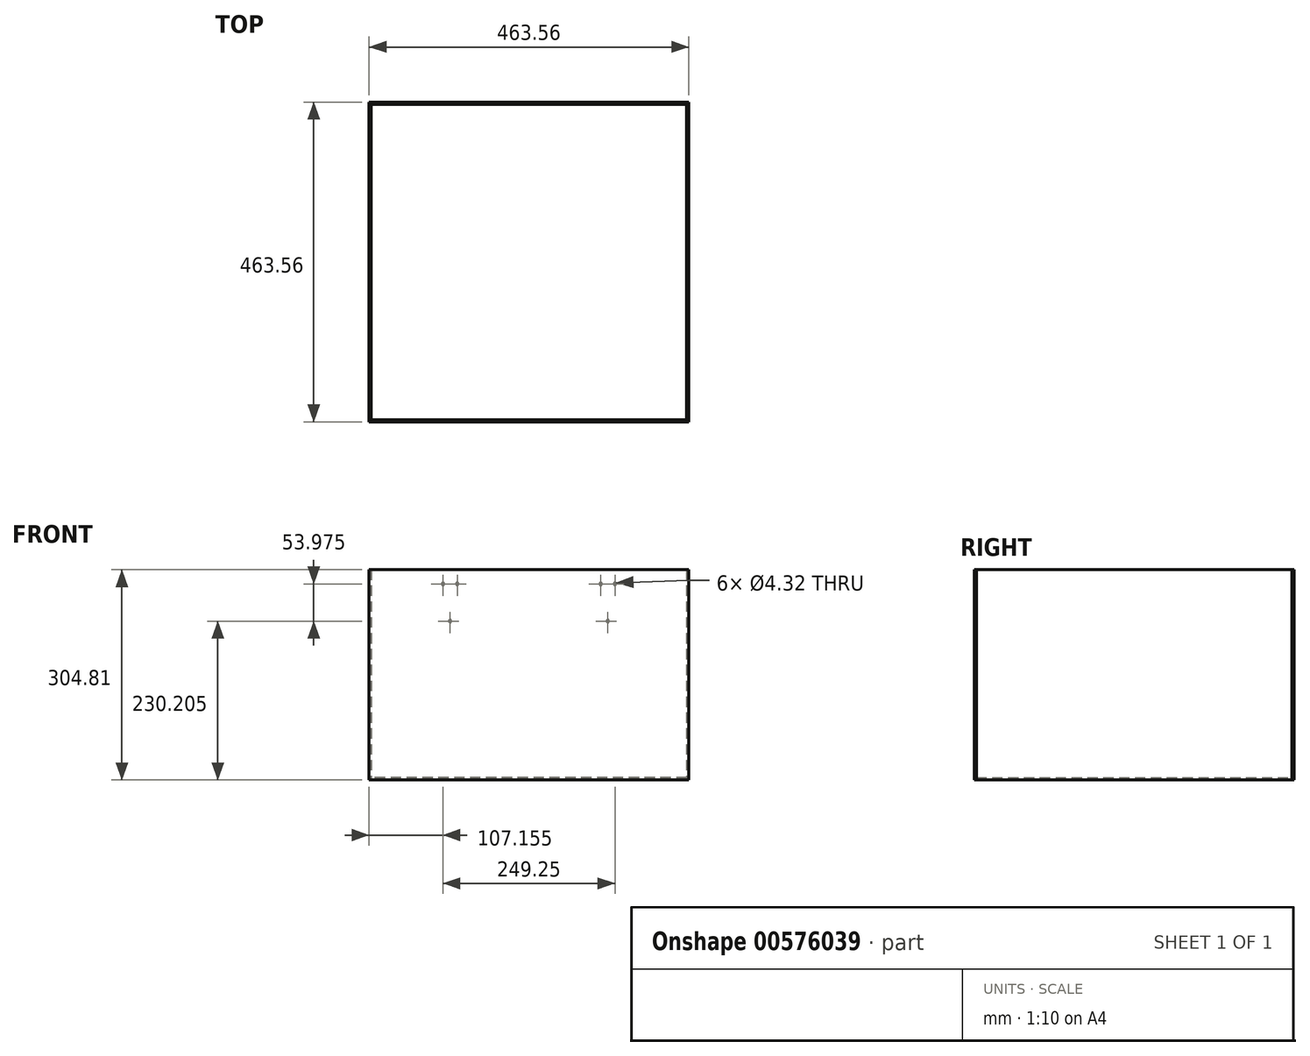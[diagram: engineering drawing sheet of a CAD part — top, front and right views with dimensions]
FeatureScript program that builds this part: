
annotation { "Feature Type Name" : "Feature", "Feature Type Description" : "" }
export const myFeature = defineFeature(function(context is Context, id is Id, definition is map)
    precondition{}
    {
        {
            var Q0;
            Q0=qCreatedBy(makeId("Top.planeOp"),FACE);
            var sketch = newSketch(context, id + "F0", { "sketchPlane" : qUnion([Q0])});
            skLineSegment(sketch, "E0.bottom", {"start": v(228.6, -228.6) * mm, "end": v(-228.6, -228.6) * mm});
            skLineSegment(sketch, "E0.top", {"start": v(228.6, 228.6) * mm, "end": v(-228.6, 228.6) * mm});
            skLineSegment(sketch, "E0.left", {"start": v(228.6, -228.6) * mm, "end": v(228.6, 228.6) * mm});
            skLineSegment(sketch, "E0.right", {"start": v(-228.6, -228.6) * mm, "end": v(-228.6, 228.6) * mm});
            skPoint(sketch, "E0.middle", {"position": v(0, 0) * mm});
            skSolve(sketch);
        }
        {
            var Q0;
            Q0=qSketchRegion(id+"F0",true);
            extrude(context, id + "F1", {"entities" : qUnion([Q0]), "depth" : 3.17 * mm, "offsetDistance" : 25.4 * mm});
        }
        {
            var Q0;
            Q0=makeQuery(id+"F1.opExtrude","SWEPT_FACE",FACE,{"disambiguationData":[OSD([sQuery(id+"F0.wireOp",EDGE,"E0.left")])]});
            var sketch = newSketch(context, id + "F2", { "sketchPlane" : qUnion([Q0])});
            skLineSegment(sketch, "E1", {"start": v(-228.6, 0) * mm, "end": v(-228.6, 3.18) * mm});
            skLineSegment(sketch, "E2", {"start": v(-228.6, 3.18) * mm, "end": v(-228.6, 307.98) * mm});
            skLineSegment(sketch, "E3", {"start": v(-228.6, 307.98) * mm, "end": v(228.6, 307.98) * mm});
            skLineSegment(sketch, "E4", {"start": v(228.6, 307.98) * mm, "end": v(228.6, 3.18) * mm});
            skLineSegment(sketch, "E5", {"start": v(228.6, 3.18) * mm, "end": v(228.6, 0) * mm});
            skLineSegment(sketch, "E6", {"start": v(228.6, 0) * mm, "end": v(-228.6, 0) * mm});
            skSolve(sketch);
        }
        {
            var Q0;
            Q0=qSketchRegion(id+"F2",true);
            extrude(context, id + "F3", {"entities" : qUnion([Q0]), "depth" : 3.17 * mm, "offsetDistance" : 25.4 * mm});
        }
        {
            var Q0;
            Q0=makeQuery(id+"F3.opExtrude","SWEPT_BODY",BODY,{"disambiguationData":[OSD([sQuery(id+"F2.wireOp",EDGE,"E1"),sQuery(id+"F2.wireOp",EDGE,"E2"),sQuery(id+"F2.wireOp",EDGE,"E3"),sQuery(id+"F2.wireOp",EDGE,"E4"),sQuery(id+"F2.wireOp",EDGE,"E5"),sQuery(id+"F2.wireOp",EDGE,"E6")])]});
            var Q1;
            Q1=qCreatedBy(makeId("Right.planeOp"),FACE);
            mirror(context, id + "F4", {"entities" : qUnion([Q0]), "mirrorPlane" : qUnion([Q1])});
        }
        {
            var Q0;
            Q0=makeQuery(id+"F1.opExtrude","SWEPT_FACE",FACE,{"disambiguationData":[OSD([sQuery(id+"F0.wireOp",EDGE,"E0.bottom")])]});
            var sketch = newSketch(context, id + "F5", { "sketchPlane" : qUnion([Q0])});
            skLineSegment(sketch, "E7", {"start": v(-231.78, 0) * mm, "end": v(-231.78, 307.98) * mm});
            skLineSegment(sketch, "E8", {"start": v(-231.78, 307.98) * mm, "end": v(231.77, 307.98) * mm});
            skLineSegment(sketch, "E9", {"start": v(231.77, 307.98) * mm, "end": v(231.77, 0) * mm});
            skLineSegment(sketch, "E10", {"start": v(-231.78, 0) * mm, "end": v(231.77, 0) * mm});
            skSolve(sketch);
        }
        {
            var Q0;
            Q0=qSketchRegion(id+"F5",true);
            extrude(context, id + "F6", {"entities" : qUnion([Q0]), "depth" : 3.17 * mm, "offsetDistance" : 25.4 * mm});
        }
        {
            var Q0;
            Q0=makeQuery(id+"F6.opExtrude","SWEPT_BODY",BODY,{"disambiguationData":[OSD([sQuery(id+"F5.wireOp",EDGE,"E7"),sQuery(id+"F5.wireOp",EDGE,"E8"),sQuery(id+"F5.wireOp",EDGE,"E9"),sQuery(id+"F5.wireOp",EDGE,"E10")])]});
            var Q1;
            Q1=qCreatedBy(makeId("Front.planeOp"),FACE);
            mirror(context, id + "F7", {"entities" : qUnion([Q0]), "mirrorPlane" : qUnion([Q1])});
        }
        {
            var Q0;
            Q0=makeQuery(id+"F7.opPattern","COPY",FACE,{"derivedFrom":makeQuery(id+"F6.opExtrude","CAP_FACE",FACE,{"disambiguationData":[OSD([sQuery(id+"F5.wireOp",EDGE,"E7"),sQuery(id+"F5.wireOp",EDGE,"E8"),sQuery(id+"F5.wireOp",EDGE,"E9"),sQuery(id+"F5.wireOp",EDGE,"E10")])],"isStart":true}),"instanceName":"1"});
            var sketch = newSketch(context, id + "F8", { "sketchPlane" : qUnion([Q0])});
            skLineSegment(sketch, "E11", {"start": v(-228.6, 307.98) * mm, "end": v(-152.4, 307.98) * mm});
            skLineSegment(sketch, "E12", {"start": v(-152.4, 307.98) * mm, "end": v(-114.3, 307.98) * mm});
            skLineSegment(sketch, "E13", {"start": v(-114.3, 307.98) * mm, "end": v(-114.3, 287.35) * mm});
            skLineSegment(sketch, "E14", {"start": v(-114.3, 287.35) * mm, "end": v(-114.3, 233.38) * mm});
            skLineSegment(sketch, "E15", {"start": v(-114.3, 287.35) * mm, "end": v(-103.97, 287.35) * mm});
            skLineSegment(sketch, "E16", {"start": v(-228.6, 307.98) * mm, "end": v(0, 307.98) * mm});
            skLineSegment(sketch, "E17", {"start": v(0, 307.98) * mm, "end": v(0, 430.1) * mm});
            skLineSegment(sketch, "E18.MirrorCS", {"start": v(-114.3, 287.35) * mm, "end": v(-124.63, 287.35) * mm});
            skLineSegment(sketch, "E19.MirrorCS", {"start": v(152.4, 307.98) * mm, "end": v(114.3, 307.98) * mm});
            skLineSegment(sketch, "E20.MirrorCS", {"start": v(228.6, 307.98) * mm, "end": v(152.4, 307.98) * mm});
            skLineSegment(sketch, "E21.MirrorCS", {"start": v(228.6, 307.98) * mm, "end": v(0, 307.98) * mm});
            skLineSegment(sketch, "E22.MirrorCS", {"start": v(114.3, 287.35) * mm, "end": v(124.63, 287.35) * mm});
            skLineSegment(sketch, "E23.MirrorCS", {"start": v(114.3, 287.35) * mm, "end": v(103.97, 287.35) * mm});
            skLineSegment(sketch, "E24.MirrorCS", {"start": v(114.3, 287.35) * mm, "end": v(114.3, 233.38) * mm});
            skLineSegment(sketch, "E25.MirrorCS", {"start": v(114.3, 307.98) * mm, "end": v(114.3, 287.35) * mm});
            skSolve(sketch);
        }
        {
            var Q0;
            Q0=sQuery(id+"F8.wireOp",VERTEX,"E23.MirrorCS.end");
            var Q1;
            Q1=sQuery(id+"F8.wireOp",VERTEX,"E22.MirrorCS.end");
            var Q2;
            Q2=sQuery(id+"F8.wireOp",VERTEX,"E24.MirrorCS.end");
            var Q3;
            Q3=sQuery(id+"F8.wireOp",VERTEX,"E14.end");
            var Q4;
            Q4=sQuery(id+"F8.wireOp",VERTEX,"E18.MirrorCS.end");
            var Q5;
            Q5=sQuery(id+"F8.wireOp",VERTEX,"E15.end");
            var Q6;
            Q6=makeQuery(id+"F7.opPattern","COPY",BODY,{"derivedFrom":makeQuery(id+"F6.opExtrude","SWEPT_BODY",BODY,{"disambiguationData":[OSD([sQuery(id+"F5.wireOp",EDGE,"E7"),sQuery(id+"F5.wireOp",EDGE,"E8"),sQuery(id+"F5.wireOp",EDGE,"E9"),sQuery(id+"F5.wireOp",EDGE,"E10")])]}),"instanceName":"1"});
            hole(context, id + "F9", {"style" : HoleStyle.SIMPLE, "endStyle" : HoleEndStyle.THROUGH, "standardTappedOrClearance" : lookupTablePath({ "standard" : "ANSI", "fit" : "Close", "size" : "#8", "type" : "Clearance" }), "standardBlindInLast" : lookupTablePath({ "fit" : "Close", "standard" : "ANSI", "size" : "#8", "type" : "Clearance" }), "holeDiameter" : 4.32 * mm, "isTappedThrough" : true, "tappedDepth" : 12.7 * mm, "tapClearance" : 3, "locations" : qUnion([Q0, Q1, Q2, Q3, Q4, Q5]), "scope" : qUnion([Q6])});
        }
        {
            var Q0;
            Q0=makeQuery(id+"F1.opExtrude","SWEPT_BODY",BODY,{"disambiguationData":[OSD([sQuery(id+"F0.wireOp",EDGE,"E0.bottom"),sQuery(id+"F0.wireOp",EDGE,"E0.top"),sQuery(id+"F0.wireOp",EDGE,"E0.left"),sQuery(id+"F0.wireOp",EDGE,"E0.right")])]});
            transform(context, id + "F10", {"entities" : qUnion([Q0]), "transformType" : TransformType.TRANSLATION_3D, "dx" : 0 * mm, "dy" : 0 * mm, "dz" : 3.17 * mm, "makeCopy" : false});
        }
        {
            var Q0;
            Q0=makeQuery(id+"F3.opExtrude","SWEPT_FACE",FACE,{"disambiguationData":[OSD([sQuery(id+"F2.wireOp",EDGE,"E6")])]});
            var Q1;
            Q1=makeQuery(id+"F6.opExtrude","SWEPT_FACE",FACE,{"disambiguationData":[OSD([sQuery(id+"F5.wireOp",EDGE,"E10")])]});
            var Q2;
            Q2=makeQuery(id+"F7.opPattern","COPY",FACE,{"derivedFrom":makeQuery(id+"F6.opExtrude","SWEPT_FACE",FACE,{"disambiguationData":[OSD([sQuery(id+"F5.wireOp",EDGE,"E10")])]}),"instanceName":"1"});
            var Q3;
            Q3=makeQuery(id+"F4.opPattern","COPY",FACE,{"derivedFrom":makeQuery(id+"F3.opExtrude","SWEPT_FACE",FACE,{"disambiguationData":[OSD([sQuery(id+"F2.wireOp",EDGE,"E6")])]}),"instanceName":"1"});
            extrude(context, id + "F11", {"entities" : qUnion([Q0, Q1, Q2, Q3]), "operationType" : NewBodyOperationType.REMOVE, "oppositeDirection" : true, "depth" : 3.17 * mm, "offsetDistance" : 25.4 * mm});
        }
    });
